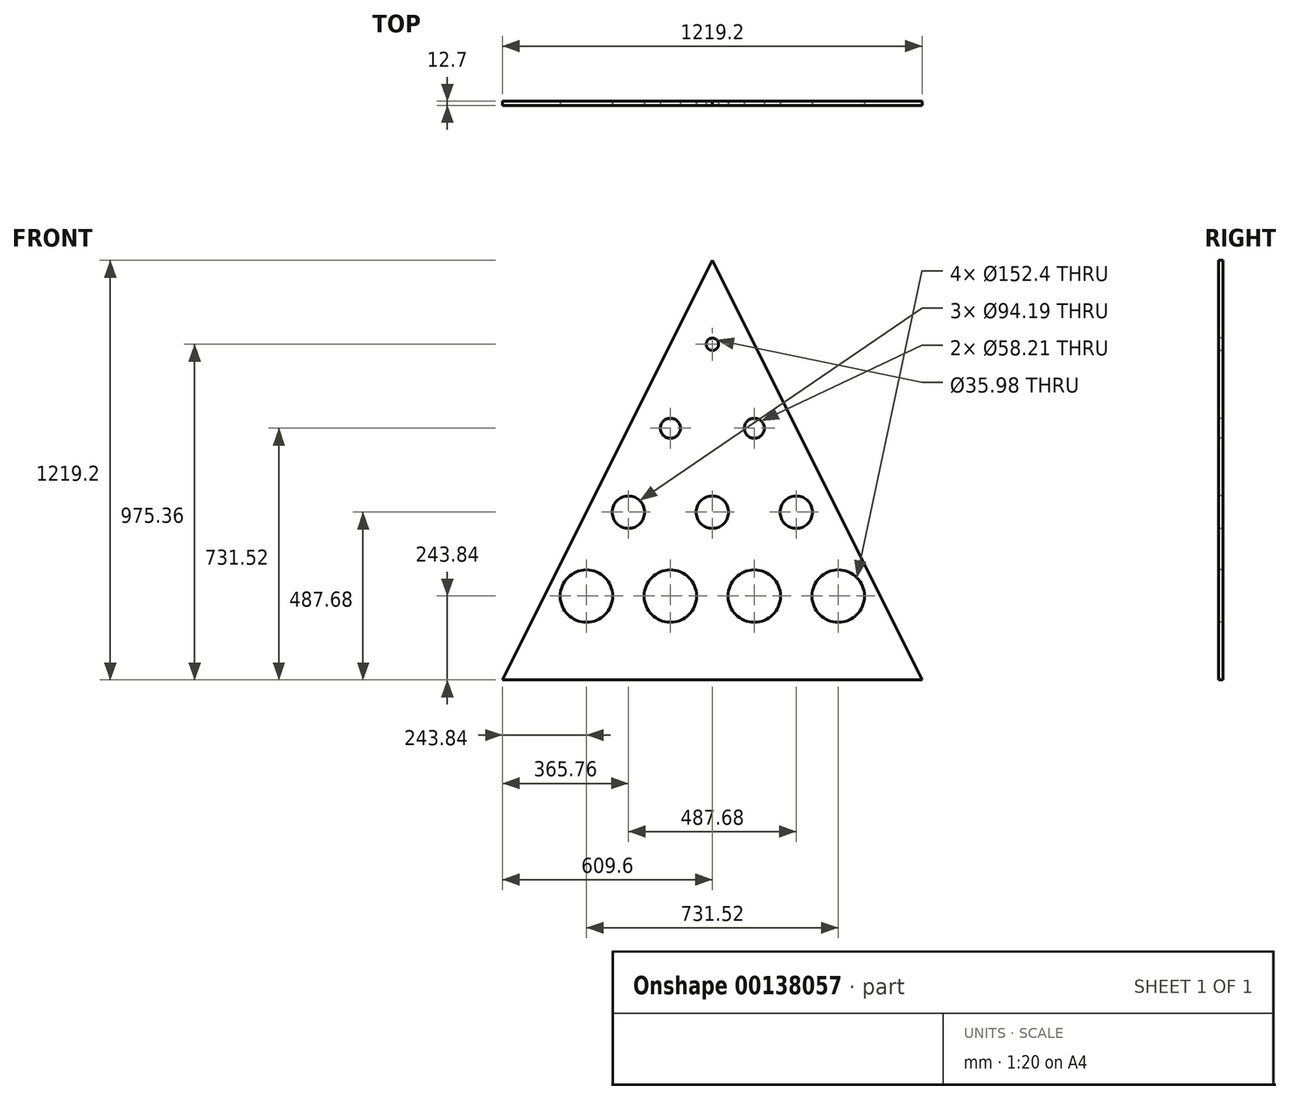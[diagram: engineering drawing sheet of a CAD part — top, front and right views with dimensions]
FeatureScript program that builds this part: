
annotation { "Feature Type Name" : "Feature", "Feature Type Description" : "" }
export const myFeature = defineFeature(function(context is Context, id is Id, definition is map)
    precondition{}
    {
        {
            var Q0;
            Q0=qCreatedBy(makeId("Front.planeOp"),FACE);
            var sketch = newSketch(context, id + "F0", { "sketchPlane" : qUnion([Q0])});
            skLineSegment(sketch, "E0.bottom", {"start": v(609.6, -609.6) * mm, "end": v(-609.6, -609.6) * mm});
            skPoint(sketch, "E0.middle", {"position": v(0, 0) * mm});
            skLineSegment(sketch, "E1", {"start": v(0, 609.6) * mm, "end": v(609.6, -609.6) * mm});
            skLineSegment(sketch, "E2", {"start": v(-609.6, -609.6) * mm, "end": v(0, 609.6) * mm});
            skSolve(sketch);
        }
        {
            var Q0;
            Q0=makeQuery(id+"F0.imprint","IMPRINT",FACE,{"disambiguationData":[TD([[makeQuery(id+"F0.imprint","IMPRINT",EDGE,{"derivedFrom":sQuery(id+"F0.wireOp",EDGE,"E0.bottom")}),-1.0]])]});
            extrude(context, id + "F1", {"entities" : qUnion([Q0]), "depth" : 12.7 * mm});
        }
        {
            var Q0;
            Q0=makeQuery(id+"F1.opExtrude","CAP_FACE",FACE,{"disambiguationData":[OSD([sQuery(id+"F0.wireOp",EDGE,"E0.bottom"),sQuery(id+"F0.wireOp",EDGE,"E1"),sQuery(id+"F0.wireOp",EDGE,"E2")])],"isStart":false});
            var sketch = newSketch(context, id + "F2", { "sketchPlane" : qUnion([Q0])});
            skLineSegment(sketch, "E3", {"start": v(0, 609.6) * mm, "end": v(0, 365.76) * mm});
            skLineSegment(sketch, "E4", {"start": v(0, 365.76) * mm, "end": v(0, 121.92) * mm});
            skLineSegment(sketch, "E5", {"start": v(0, 121.92) * mm, "end": v(0, -121.92) * mm});
            skLineSegment(sketch, "E6", {"start": v(0, -121.92) * mm, "end": v(0, -365.76) * mm});
            skLineSegment(sketch, "E7", {"start": v(0, -365.76) * mm, "end": v(0, -609.6) * mm});
            skLineSegment(sketch, "E8", {"start": v(0, 365.76) * mm, "end": v(-365.76, -365.76) * mm});
            skLineSegment(sketch, "E9", {"start": v(0, 365.76) * mm, "end": v(365.76, -365.76) * mm});
            skLineSegment(sketch, "E10", {"start": v(0, 121.92) * mm, "end": v(-121.92, 121.92) * mm});
            skLineSegment(sketch, "E11", {"start": v(0, 121.92) * mm, "end": v(121.92, 121.92) * mm});
            skLineSegment(sketch, "E12", {"start": v(0, -121.92) * mm, "end": v(-243.84, -121.92) * mm});
            skLineSegment(sketch, "E13", {"start": v(0, -121.92) * mm, "end": v(243.84, -121.92) * mm});
            skLineSegment(sketch, "E14", {"start": v(-365.76, -365.76) * mm, "end": v(-121.92, -365.76) * mm});
            skLineSegment(sketch, "E15", {"start": v(-121.92, -365.76) * mm, "end": v(121.92, -365.76) * mm});
            skLineSegment(sketch, "E16", {"start": v(121.92, -365.76) * mm, "end": v(365.76, -365.76) * mm});
            skCircle(sketch, "E17", {"center": v(-365.76, -365.76) * mm, "radius": 76.2 * mm});
            skCircle(sketch, "E18", {"center": v(121.92, -365.76) * mm, "radius": 76.2 * mm});
            skCircle(sketch, "E19", {"center": v(365.76, -365.76) * mm, "radius": 76.2 * mm});
            skCircle(sketch, "E20", {"center": v(-121.92, -365.76) * mm, "radius": 76.2 * mm});
            skCircle(sketch, "E21", {"center": v(-243.84, -121.92) * mm, "radius": 47.1 * mm});
            skCircle(sketch, "E22", {"center": v(0, -121.92) * mm, "radius": 47.1 * mm});
            skCircle(sketch, "E23", {"center": v(243.84, -121.92) * mm, "radius": 47.1 * mm});
            skCircle(sketch, "E24", {"center": v(-121.92, 121.92) * mm, "radius": 29.1 * mm});
            skCircle(sketch, "E25", {"center": v(121.92, 121.92) * mm, "radius": 29.1 * mm});
            skCircle(sketch, "E26", {"center": v(0, 365.76) * mm, "radius": 17.99 * mm});
            skSolve(sketch);
        }
        {
            var Q0;
            {var subQ1=sQuery(id+"F2.wireOp",EDGE,"E3");var subQ3=sQuery(id+"F2.wireOp",EDGE,"E26");var subQ4=makeQuery(id+"F2.imprint","INTERSECT",VERTEX,{"derivedFrom":[subQ1,subQ3]});Q0=makeQuery(id+"F2.imprint","IMPRINT",FACE,{"disambiguationData":[TD([[makeQuery(id+"F2.imprint","IMPRINT",EDGE,{"disambiguationData":[TD([[subQ4,-1.0]])],"derivedFrom":subQ3}),1.0]])]});}
            var Q1;
            {var subQ1=sQuery(id+"F2.wireOp",EDGE,"E3");var subQ3=sQuery(id+"F2.wireOp",EDGE,"E26");var subQ4=makeQuery(id+"F2.imprint","INTERSECT",VERTEX,{"derivedFrom":[subQ1,subQ3]});Q1=makeQuery(id+"F2.imprint","IMPRINT",FACE,{"disambiguationData":[TD([[makeQuery(id+"F2.imprint","IMPRINT",EDGE,{"disambiguationData":[TD([[subQ4,1.0]])],"derivedFrom":subQ3}),1.0]])]});}
            var Q2;
            {var subQ1=sQuery(id+"F2.wireOp",EDGE,"E4");var subQ3=sQuery(id+"F2.wireOp",EDGE,"E26");var subQ4=makeQuery(id+"F2.imprint","INTERSECT",VERTEX,{"derivedFrom":[subQ1,subQ3]});Q2=makeQuery(id+"F2.imprint","IMPRINT",FACE,{"disambiguationData":[TD([[makeQuery(id+"F2.imprint","IMPRINT",EDGE,{"disambiguationData":[TD([[subQ4,-1.0]])],"derivedFrom":subQ3}),1.0]])]});}
            var Q3;
            {var subQ1=sQuery(id+"F2.wireOp",EDGE,"E4");var subQ3=sQuery(id+"F2.wireOp",EDGE,"E26");var subQ4=makeQuery(id+"F2.imprint","INTERSECT",VERTEX,{"derivedFrom":[subQ1,subQ3]});Q3=makeQuery(id+"F2.imprint","IMPRINT",FACE,{"disambiguationData":[TD([[makeQuery(id+"F2.imprint","IMPRINT",EDGE,{"disambiguationData":[TD([[subQ4,1.0]])],"derivedFrom":subQ3}),1.0]])]});}
            var Q4;
            {var subQ0=sQuery(id+"F2.wireOp",EDGE,"E8");var subQ1=makeQuery(id+"F2.imprint","INTERSECT",VERTEX,{"derivedFrom":[subQ0,sQuery(id+"F2.wireOp",EDGE,"E10")]});Q4=makeQuery(id+"F2.imprint","IMPRINT",FACE,{"disambiguationData":[TD([[makeQuery(id+"F2.imprint","IMPRINT",EDGE,{"disambiguationData":[TD([[subQ1,1.0]])],"derivedFrom":subQ0}),-1.0]])]});}
            var Q5;
            {var subQ0=sQuery(id+"F2.wireOp",EDGE,"E10");var subQ1=sQuery(id+"F2.wireOp",EDGE,"E8");var subQ2=makeQuery(id+"F2.imprint","INTERSECT",VERTEX,{"derivedFrom":[subQ1,subQ0]});Q5=makeQuery(id+"F2.imprint","IMPRINT",FACE,{"disambiguationData":[TD([[makeQuery(id+"F2.imprint","IMPRINT",EDGE,{"disambiguationData":[TD([[subQ2,1.0]])],"derivedFrom":subQ1}),1.0]])]});}
            var Q6;
            {var subQ0=sQuery(id+"F2.wireOp",EDGE,"E10");var subQ1=sQuery(id+"F2.wireOp",EDGE,"E8");var subQ2=makeQuery(id+"F2.imprint","INTERSECT",VERTEX,{"derivedFrom":[subQ1,subQ0]});Q6=makeQuery(id+"F2.imprint","IMPRINT",FACE,{"disambiguationData":[TD([[makeQuery(id+"F2.imprint","IMPRINT",EDGE,{"disambiguationData":[TD([[subQ2,-1.0]])],"derivedFrom":subQ1}),1.0]])]});}
            var Q7;
            {var subQ0=sQuery(id+"F2.wireOp",EDGE,"E9");var subQ1=makeQuery(id+"F2.imprint","INTERSECT",VERTEX,{"derivedFrom":[subQ0,sQuery(id+"F2.wireOp",EDGE,"E11")]});Q7=makeQuery(id+"F2.imprint","IMPRINT",FACE,{"disambiguationData":[TD([[makeQuery(id+"F2.imprint","IMPRINT",EDGE,{"disambiguationData":[TD([[subQ1,1.0]])],"derivedFrom":subQ0}),1.0]])]});}
            var Q8;
            {var subQ0=sQuery(id+"F2.wireOp",EDGE,"E11");var subQ1=sQuery(id+"F2.wireOp",EDGE,"E9");var subQ2=makeQuery(id+"F2.imprint","INTERSECT",VERTEX,{"derivedFrom":[subQ1,subQ0]});Q8=makeQuery(id+"F2.imprint","IMPRINT",FACE,{"disambiguationData":[TD([[makeQuery(id+"F2.imprint","IMPRINT",EDGE,{"disambiguationData":[TD([[subQ2,1.0]])],"derivedFrom":subQ1}),-1.0]])]});}
            var Q9;
            {var subQ0=sQuery(id+"F2.wireOp",EDGE,"E11");var subQ1=sQuery(id+"F2.wireOp",EDGE,"E9");var subQ2=makeQuery(id+"F2.imprint","INTERSECT",VERTEX,{"derivedFrom":[subQ1,subQ0]});Q9=makeQuery(id+"F2.imprint","IMPRINT",FACE,{"disambiguationData":[TD([[makeQuery(id+"F2.imprint","IMPRINT",EDGE,{"disambiguationData":[TD([[subQ2,-1.0]])],"derivedFrom":subQ1}),-1.0]])]});}
            var Q10;
            {var subQ0=sQuery(id+"F2.wireOp",EDGE,"E14");var subQ1=sQuery(id+"F2.wireOp",EDGE,"E8");var subQ2=makeQuery(id+"F2.imprint","INTERSECT",VERTEX,{"derivedFrom":[subQ1,subQ0]});Q10=makeQuery(id+"F2.imprint","IMPRINT",FACE,{"disambiguationData":[TD([[makeQuery(id+"F2.imprint","IMPRINT",EDGE,{"disambiguationData":[TD([[subQ2,1.0]])],"derivedFrom":subQ1}),-1.0]])]});}
            var Q11;
            {var subQ0=sQuery(id+"F2.wireOp",EDGE,"E14");var subQ1=sQuery(id+"F2.wireOp",EDGE,"E8");var subQ2=makeQuery(id+"F2.imprint","INTERSECT",VERTEX,{"derivedFrom":[subQ1,subQ0]});Q11=makeQuery(id+"F2.imprint","IMPRINT",FACE,{"disambiguationData":[TD([[makeQuery(id+"F2.imprint","IMPRINT",EDGE,{"disambiguationData":[TD([[subQ2,1.0]])],"derivedFrom":subQ1}),1.0]])]});}
            var Q12;
            {var subQ0=sQuery(id+"F2.wireOp",EDGE,"E12");var subQ1=sQuery(id+"F2.wireOp",EDGE,"E8");var subQ2=makeQuery(id+"F2.imprint","INTERSECT",VERTEX,{"derivedFrom":[subQ1,subQ0]});Q12=makeQuery(id+"F2.imprint","IMPRINT",FACE,{"disambiguationData":[TD([[makeQuery(id+"F2.imprint","IMPRINT",EDGE,{"disambiguationData":[TD([[subQ2,-1.0]])],"derivedFrom":subQ1}),1.0]])]});}
            var Q13;
            {var subQ0=sQuery(id+"F2.wireOp",EDGE,"E12");var subQ1=sQuery(id+"F2.wireOp",EDGE,"E8");var subQ2=makeQuery(id+"F2.imprint","INTERSECT",VERTEX,{"derivedFrom":[subQ1,subQ0]});Q13=makeQuery(id+"F2.imprint","IMPRINT",FACE,{"disambiguationData":[TD([[makeQuery(id+"F2.imprint","IMPRINT",EDGE,{"disambiguationData":[TD([[subQ2,1.0]])],"derivedFrom":subQ1}),1.0]])]});}
            var Q14;
            {var subQ0=sQuery(id+"F2.wireOp",EDGE,"E8");var subQ1=makeQuery(id+"F2.imprint","INTERSECT",VERTEX,{"derivedFrom":[subQ0,sQuery(id+"F2.wireOp",EDGE,"E12")]});Q14=makeQuery(id+"F2.imprint","IMPRINT",FACE,{"disambiguationData":[TD([[makeQuery(id+"F2.imprint","IMPRINT",EDGE,{"disambiguationData":[TD([[subQ1,1.0]])],"derivedFrom":subQ0}),-1.0]])]});}
            var Q15;
            {var subQ1=sQuery(id+"F2.wireOp",EDGE,"E5");var subQ3=sQuery(id+"F2.wireOp",EDGE,"E22");var subQ4=makeQuery(id+"F2.imprint","INTERSECT",VERTEX,{"derivedFrom":[subQ1,subQ3]});Q15=makeQuery(id+"F2.imprint","IMPRINT",FACE,{"disambiguationData":[TD([[makeQuery(id+"F2.imprint","IMPRINT",EDGE,{"disambiguationData":[TD([[subQ4,1.0]])],"derivedFrom":subQ3}),1.0]])]});}
            var Q16;
            {var subQ1=sQuery(id+"F2.wireOp",EDGE,"E5");var subQ3=sQuery(id+"F2.wireOp",EDGE,"E22");var subQ4=makeQuery(id+"F2.imprint","INTERSECT",VERTEX,{"derivedFrom":[subQ1,subQ3]});Q16=makeQuery(id+"F2.imprint","IMPRINT",FACE,{"disambiguationData":[TD([[makeQuery(id+"F2.imprint","IMPRINT",EDGE,{"disambiguationData":[TD([[subQ4,-1.0]])],"derivedFrom":subQ3}),1.0]])]});}
            var Q17;
            {var subQ1=sQuery(id+"F2.wireOp",EDGE,"E6");var subQ3=sQuery(id+"F2.wireOp",EDGE,"E22");var subQ4=makeQuery(id+"F2.imprint","INTERSECT",VERTEX,{"derivedFrom":[subQ1,subQ3]});Q17=makeQuery(id+"F2.imprint","IMPRINT",FACE,{"disambiguationData":[TD([[makeQuery(id+"F2.imprint","IMPRINT",EDGE,{"disambiguationData":[TD([[subQ4,1.0]])],"derivedFrom":subQ3}),1.0]])]});}
            var Q18;
            {var subQ1=sQuery(id+"F2.wireOp",EDGE,"E6");var subQ3=sQuery(id+"F2.wireOp",EDGE,"E22");var subQ4=makeQuery(id+"F2.imprint","INTERSECT",VERTEX,{"derivedFrom":[subQ1,subQ3]});Q18=makeQuery(id+"F2.imprint","IMPRINT",FACE,{"disambiguationData":[TD([[makeQuery(id+"F2.imprint","IMPRINT",EDGE,{"disambiguationData":[TD([[subQ4,-1.0]])],"derivedFrom":subQ3}),1.0]])]});}
            var Q19;
            {var subQ0=sQuery(id+"F2.wireOp",EDGE,"E13");var subQ1=sQuery(id+"F2.wireOp",EDGE,"E9");var subQ2=makeQuery(id+"F2.imprint","INTERSECT",VERTEX,{"derivedFrom":[subQ1,subQ0]});Q19=makeQuery(id+"F2.imprint","IMPRINT",FACE,{"disambiguationData":[TD([[makeQuery(id+"F2.imprint","IMPRINT",EDGE,{"disambiguationData":[TD([[subQ2,1.0]])],"derivedFrom":subQ1}),-1.0]])]});}
            var Q20;
            {var subQ0=sQuery(id+"F2.wireOp",EDGE,"E9");var subQ1=makeQuery(id+"F2.imprint","INTERSECT",VERTEX,{"derivedFrom":[subQ0,sQuery(id+"F2.wireOp",EDGE,"E13")]});Q20=makeQuery(id+"F2.imprint","IMPRINT",FACE,{"disambiguationData":[TD([[makeQuery(id+"F2.imprint","IMPRINT",EDGE,{"disambiguationData":[TD([[subQ1,1.0]])],"derivedFrom":subQ0}),1.0]])]});}
            var Q21;
            {var subQ0=sQuery(id+"F2.wireOp",EDGE,"E13");var subQ1=sQuery(id+"F2.wireOp",EDGE,"E9");var subQ2=makeQuery(id+"F2.imprint","INTERSECT",VERTEX,{"derivedFrom":[subQ1,subQ0]});Q21=makeQuery(id+"F2.imprint","IMPRINT",FACE,{"disambiguationData":[TD([[makeQuery(id+"F2.imprint","IMPRINT",EDGE,{"disambiguationData":[TD([[subQ2,-1.0]])],"derivedFrom":subQ1}),-1.0]])]});}
            var Q22;
            {var subQ0=sQuery(id+"F2.wireOp",EDGE,"E16");var subQ1=sQuery(id+"F2.wireOp",EDGE,"E9");var subQ2=makeQuery(id+"F2.imprint","INTERSECT",VERTEX,{"derivedFrom":[subQ1,subQ0]});Q22=makeQuery(id+"F2.imprint","IMPRINT",FACE,{"disambiguationData":[TD([[makeQuery(id+"F2.imprint","IMPRINT",EDGE,{"disambiguationData":[TD([[subQ2,1.0]])],"derivedFrom":subQ1}),1.0]])]});}
            var Q23;
            {var subQ0=sQuery(id+"F2.wireOp",EDGE,"E16");var subQ1=sQuery(id+"F2.wireOp",EDGE,"E9");var subQ2=makeQuery(id+"F2.imprint","INTERSECT",VERTEX,{"derivedFrom":[subQ1,subQ0]});Q23=makeQuery(id+"F2.imprint","IMPRINT",FACE,{"disambiguationData":[TD([[makeQuery(id+"F2.imprint","IMPRINT",EDGE,{"disambiguationData":[TD([[subQ2,1.0]])],"derivedFrom":subQ1}),-1.0]])]});}
            var Q24;
            {var subQ0=sQuery(id+"F2.wireOp",EDGE,"E16");var subQ1=sQuery(id+"F2.wireOp",EDGE,"E15");var subQ2=makeQuery(id+"F2.imprint","INTERSECT",VERTEX,{"derivedFrom":[subQ1,subQ0]});Q24=makeQuery(id+"F2.imprint","IMPRINT",FACE,{"disambiguationData":[TD([[makeQuery(id+"F2.imprint","IMPRINT",EDGE,{"disambiguationData":[TD([[subQ2,1.0]])],"derivedFrom":subQ1}),1.0]])]});}
            var Q25;
            {var subQ0=sQuery(id+"F2.wireOp",EDGE,"E16");var subQ1=sQuery(id+"F2.wireOp",EDGE,"E15");var subQ2=makeQuery(id+"F2.imprint","INTERSECT",VERTEX,{"derivedFrom":[subQ1,subQ0]});Q25=makeQuery(id+"F2.imprint","IMPRINT",FACE,{"disambiguationData":[TD([[makeQuery(id+"F2.imprint","IMPRINT",EDGE,{"disambiguationData":[TD([[subQ2,1.0]])],"derivedFrom":subQ1}),-1.0]])]});}
            var Q26;
            {var subQ0=sQuery(id+"F2.wireOp",EDGE,"E15");var subQ1=sQuery(id+"F2.wireOp",EDGE,"E14");var subQ2=makeQuery(id+"F2.imprint","INTERSECT",VERTEX,{"derivedFrom":[subQ1,subQ0]});Q26=makeQuery(id+"F2.imprint","IMPRINT",FACE,{"disambiguationData":[TD([[makeQuery(id+"F2.imprint","IMPRINT",EDGE,{"disambiguationData":[TD([[subQ2,1.0]])],"derivedFrom":subQ1}),-1.0]])]});}
            var Q27;
            {var subQ0=sQuery(id+"F2.wireOp",EDGE,"E15");var subQ1=sQuery(id+"F2.wireOp",EDGE,"E14");var subQ2=makeQuery(id+"F2.imprint","INTERSECT",VERTEX,{"derivedFrom":[subQ1,subQ0]});Q27=makeQuery(id+"F2.imprint","IMPRINT",FACE,{"disambiguationData":[TD([[makeQuery(id+"F2.imprint","IMPRINT",EDGE,{"disambiguationData":[TD([[subQ2,1.0]])],"derivedFrom":subQ1}),1.0]])]});}
            extrude(context, id + "F3", {"entities" : qUnion([Q0, Q1, Q2, Q3, Q4, Q5, Q6, Q7, Q8, Q9, Q10, Q11, Q12, Q13, Q14, Q15, Q16, Q17, Q18, Q19, Q20, Q21, Q22, Q23, Q24, Q25, Q26, Q27]), "operationType" : NewBodyOperationType.REMOVE, "oppositeDirection" : true, "depth" : 12.7 * mm});
        }
    });
